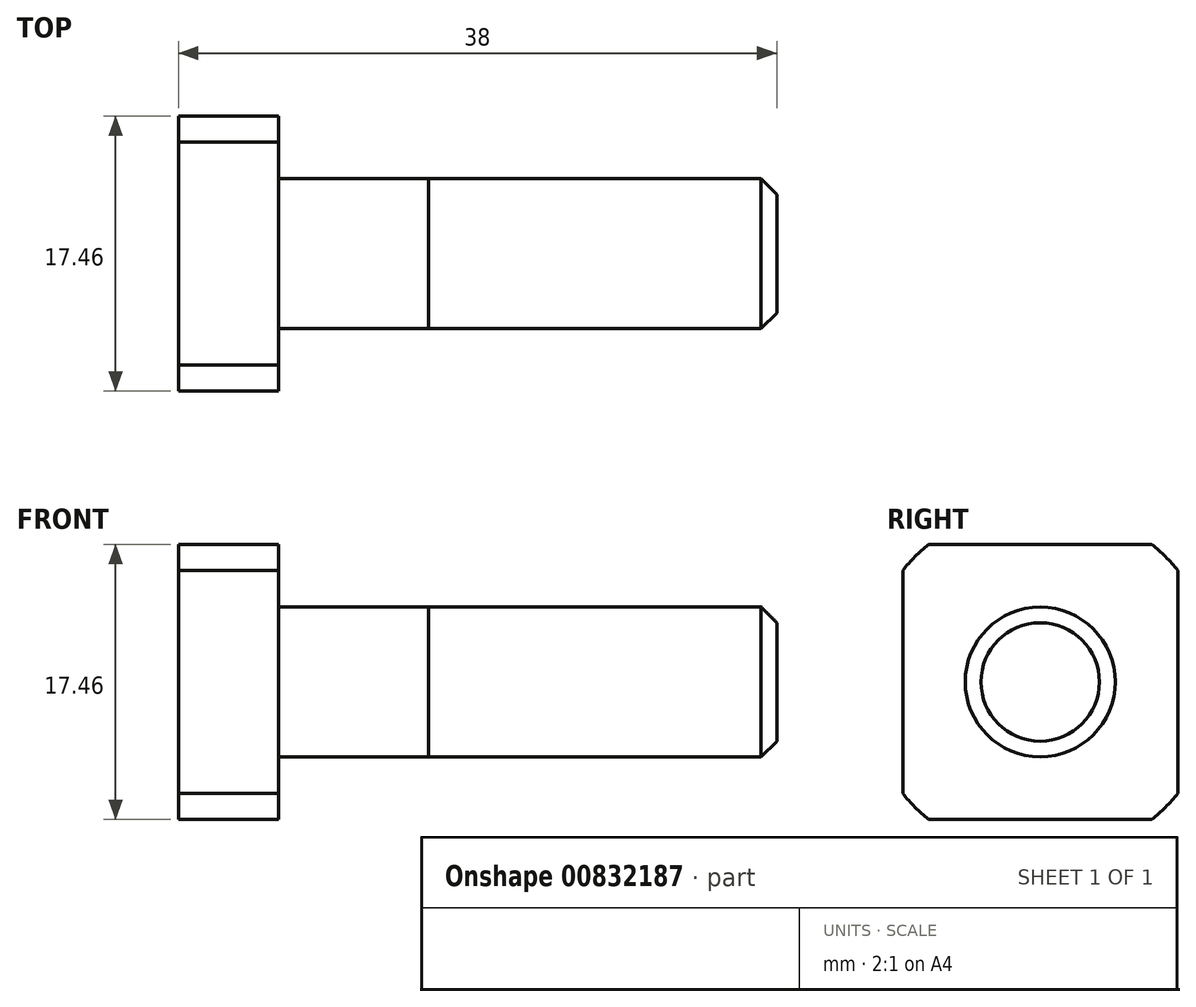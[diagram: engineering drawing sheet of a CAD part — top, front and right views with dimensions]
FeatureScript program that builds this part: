
annotation { "Feature Type Name" : "Feature", "Feature Type Description" : "" }
export const myFeature = defineFeature(function(context is Context, id is Id, definition is map)
    precondition{}
    {
        {
            var Q0;
            Q0=qCreatedBy(makeId("Front.planeOp"),FACE);
            var sketch = newSketch(context, id + "F0", { "sketchPlane" : qUnion([Q0])});
            skLineSegment(sketch, "E0", {"start": v(0, 0) * mm, "end": v(38, 0) * mm});
            skLineSegment(sketch, "E1", {"start": v(38, 0) * mm, "end": v(38, 4.76) * mm});
            skLineSegment(sketch, "E2", {"start": v(38, 4.76) * mm, "end": v(15.88, 4.76) * mm});
            skLineSegment(sketch, "E3", {"start": v(6.35, 4.76) * mm, "end": v(6.35, 11.25) * mm});
            skLineSegment(sketch, "E4", {"start": v(6.35, 11.25) * mm, "end": v(0, 11.25) * mm});
            skLineSegment(sketch, "E5", {"start": v(0, 11.25) * mm, "end": v(0, 0) * mm});
            skLineSegment(sketch, "E6", {"start": v(6.35, 4.76) * mm, "end": v(15.88, 4.76) * mm});
            skLineSegment(sketch, "E7", {"start": v(15.88, 4.76) * mm, "end": v(15.88, 4.76) * mm});
            skSolve(sketch);
        }
        {
            var Q0;
            Q0=makeQuery(id+"F0.imprint","IMPRINT",FACE,{"disambiguationData":[TD([[makeQuery(id+"F0.imprint","IMPRINT",EDGE,{"derivedFrom":sQuery(id+"F0.wireOp",EDGE,"E0")}),1.0]])]});
            var Q1;
            Q1=qSketchRegion(id+"F0",true);
            var Q2;
            Q2=makeQuery(id+"F0.imprint","IMPRINT",FACE,{"disambiguationData":[TD([[makeQuery(id+"F0.imprint","IMPRINT",EDGE,{"derivedFrom":sQuery(id+"F0.wireOp",EDGE,"E0")}),1.0]])]});
            var Q3;
            Q3=makeQuery(id+"F0.imprint","IMPRINT",FACE,{"disambiguationData":[TD([[makeQuery(id+"F0.imprint","IMPRINT",EDGE,{"derivedFrom":sQuery(id+"F0.wireOp",EDGE,"E0")}),1.0]])]});
            var Q4;
            Q4=sQuery(id+"F0.wireOp",EDGE,"E0");
            revolve(context, id + "F1", {"surfaceOperationType" : NewSurfaceOperationType.NEW, "entities" : qUnion([Q0, Q1, Q2, Q3]), "axis" : qUnion([Q4]), "revolveType" : RevolveType.FULL});
        }
        {
            var Q0;
            Q0=makeQuery(id+"F1.opRevolve","SWEPT_FACE",FACE,{"disambiguationData":[OSD([sQuery(id+"F0.wireOp",EDGE,"E5")])]});
            var sketch = newSketch(context, id + "F2", { "sketchPlane" : qUnion([Q0])});
            skLineSegment(sketch, "E8.bottom", {"start": v(-8.73, 7.1) * mm, "end": v(-11.25, 7.1) * mm});
            skLineSegment(sketch, "E8.top", {"start": v(-8.73, -7.1) * mm, "end": v(-11.25, -7.1) * mm});
            skLineSegment(sketch, "E8.left", {"start": v(-8.73, 7.1) * mm, "end": v(-8.73, -7.1) * mm});
            skLineSegment(sketch, "E8.right", {"start": v(-11.25, 7.1) * mm, "end": v(-11.25, -7.1) * mm});
            skLineSegment(sketch, "E9.bottom", {"start": v(8.73, 7.1) * mm, "end": v(11.25, 7.1) * mm});
            skLineSegment(sketch, "E9.top", {"start": v(8.73, -7.1) * mm, "end": v(11.25, -7.1) * mm});
            skLineSegment(sketch, "E9.left", {"start": v(8.73, 7.1) * mm, "end": v(8.73, -7.1) * mm});
            skLineSegment(sketch, "E9.right", {"start": v(11.25, 7.1) * mm, "end": v(11.25, -7.1) * mm});
            skLineSegment(sketch, "E10.bottom", {"start": v(-7.1, 8.73) * mm, "end": v(7.1, 8.73) * mm});
            skLineSegment(sketch, "E10.top", {"start": v(-7.1, 11.25) * mm, "end": v(7.1, 11.25) * mm});
            skLineSegment(sketch, "E10.left", {"start": v(-7.1, 8.73) * mm, "end": v(-7.1, 11.25) * mm});
            skLineSegment(sketch, "E10.right", {"start": v(7.1, 8.73) * mm, "end": v(7.1, 11.25) * mm});
            skLineSegment(sketch, "E11.bottom", {"start": v(-7.1, -8.73) * mm, "end": v(7.1, -8.73) * mm});
            skLineSegment(sketch, "E11.top", {"start": v(-7.1, -11.25) * mm, "end": v(7.1, -11.25) * mm});
            skLineSegment(sketch, "E11.left", {"start": v(-7.1, -8.73) * mm, "end": v(-7.1, -11.25) * mm});
            skLineSegment(sketch, "E11.right", {"start": v(7.1, -8.73) * mm, "end": v(7.1, -11.25) * mm});
            skLineSegment(sketch, "E12", {"start": v(0, 8.73) * mm, "end": v(0, -8.73) * mm, "construction": true});
            skLineSegment(sketch, "E13", {"start": v(-8.73, 0) * mm, "end": v(8.73, 0) * mm, "construction": true});
            skSolve(sketch);
        }
        {
            var Q0;
            Q0=qSketchRegion(id+"F2",true);
            var Q1;
            Q1=makeQuery(id+"F1.opRevolve","SWEPT_FACE",FACE,{"disambiguationData":[OSD([sQuery(id+"F0.wireOp",EDGE,"E3")])]});
            extrude(context, id + "F3", {"entities" : qUnion([Q0]), "operationType" : NewBodyOperationType.REMOVE, "endBound" : BoundingType.UP_TO_SURFACE, "oppositeDirection" : true, "depth" : 25 * mm, "endBoundEntityFace" : qUnion([Q1]), "offsetDistance" : 25 * mm});
        }
        {
            var Q0;
            Q0=makeQuery(id+"F1.opRevolve","SWEPT_EDGE",EDGE,{"disambiguationData":[OSD([sQuery(id+"F0.wireOp",EDGE,"E1"),sQuery(id+"F0.wireOp",EDGE,"E2")])]});
            chamfer(context, id + "F4", {"entities" : qUnion([Q0]), "width" : 1 * mm, "tangentPropagation" : true});
        }
    });
